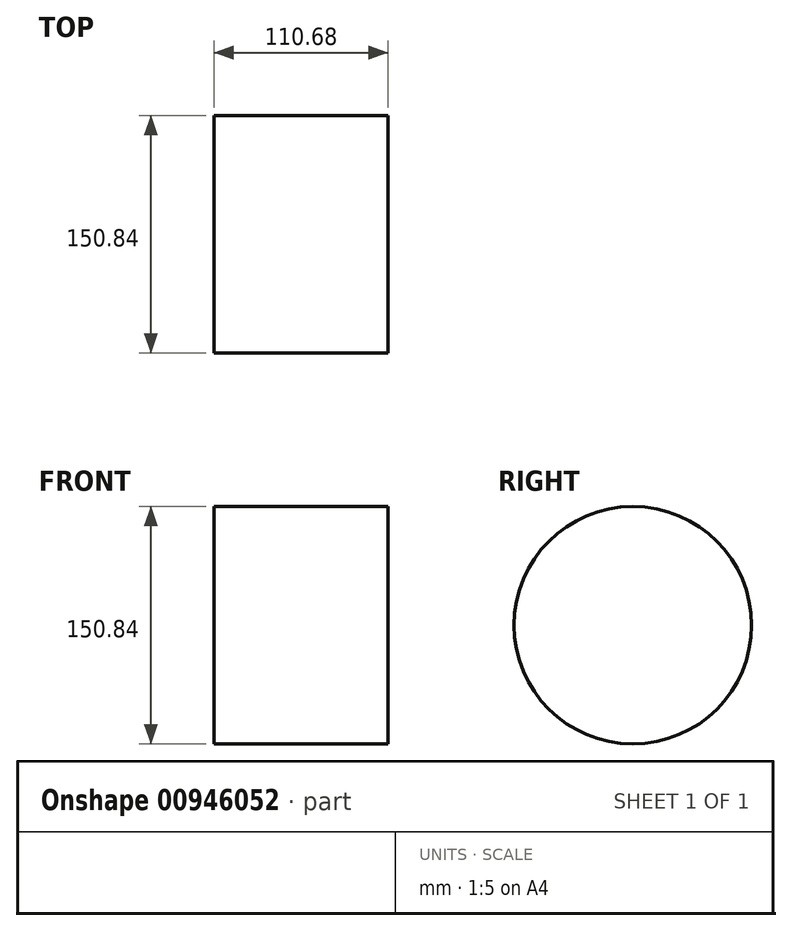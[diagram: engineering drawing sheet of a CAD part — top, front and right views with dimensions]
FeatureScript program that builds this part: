
annotation { "Feature Type Name" : "Feature", "Feature Type Description" : "" }
export const myFeature = defineFeature(function(context is Context, id is Id, definition is map)
    precondition{}
    {
        {
            var Q0;
            Q0=qCreatedBy(makeId("Front.planeOp"),FACE);
            var sketch = newSketch(context, id + "F0", { "sketchPlane" : qUnion([Q0])});
            skLineSegment(sketch, "E0.bottom", {"start": v(-52.33, 38.36) * mm, "end": v(58.35, 38.36) * mm});
            skLineSegment(sketch, "E0.top", {"start": v(-52.33, -37.06) * mm, "end": v(58.35, -37.06) * mm});
            skLineSegment(sketch, "E0.left", {"start": v(-52.33, 38.36) * mm, "end": v(-52.33, -37.06) * mm});
            skLineSegment(sketch, "E0.right", {"start": v(58.35, 38.36) * mm, "end": v(58.35, -37.06) * mm});
            skSolve(sketch);
        }
        {
            var Q0;
            Q0 = qSketchRegion(id + "F0", true);
            var Q1;
            Q1=sQuery(id+"F0.wireOp",EDGE,"E0.bottom");
            revolve(context, id + "F1", {"surfaceOperationType" : NewSurfaceOperationType.NEW, "entities" : qUnion([Q0]), "axis" : qUnion([Q1]), "revolveType" : RevolveType.FULL});
        }
    });
